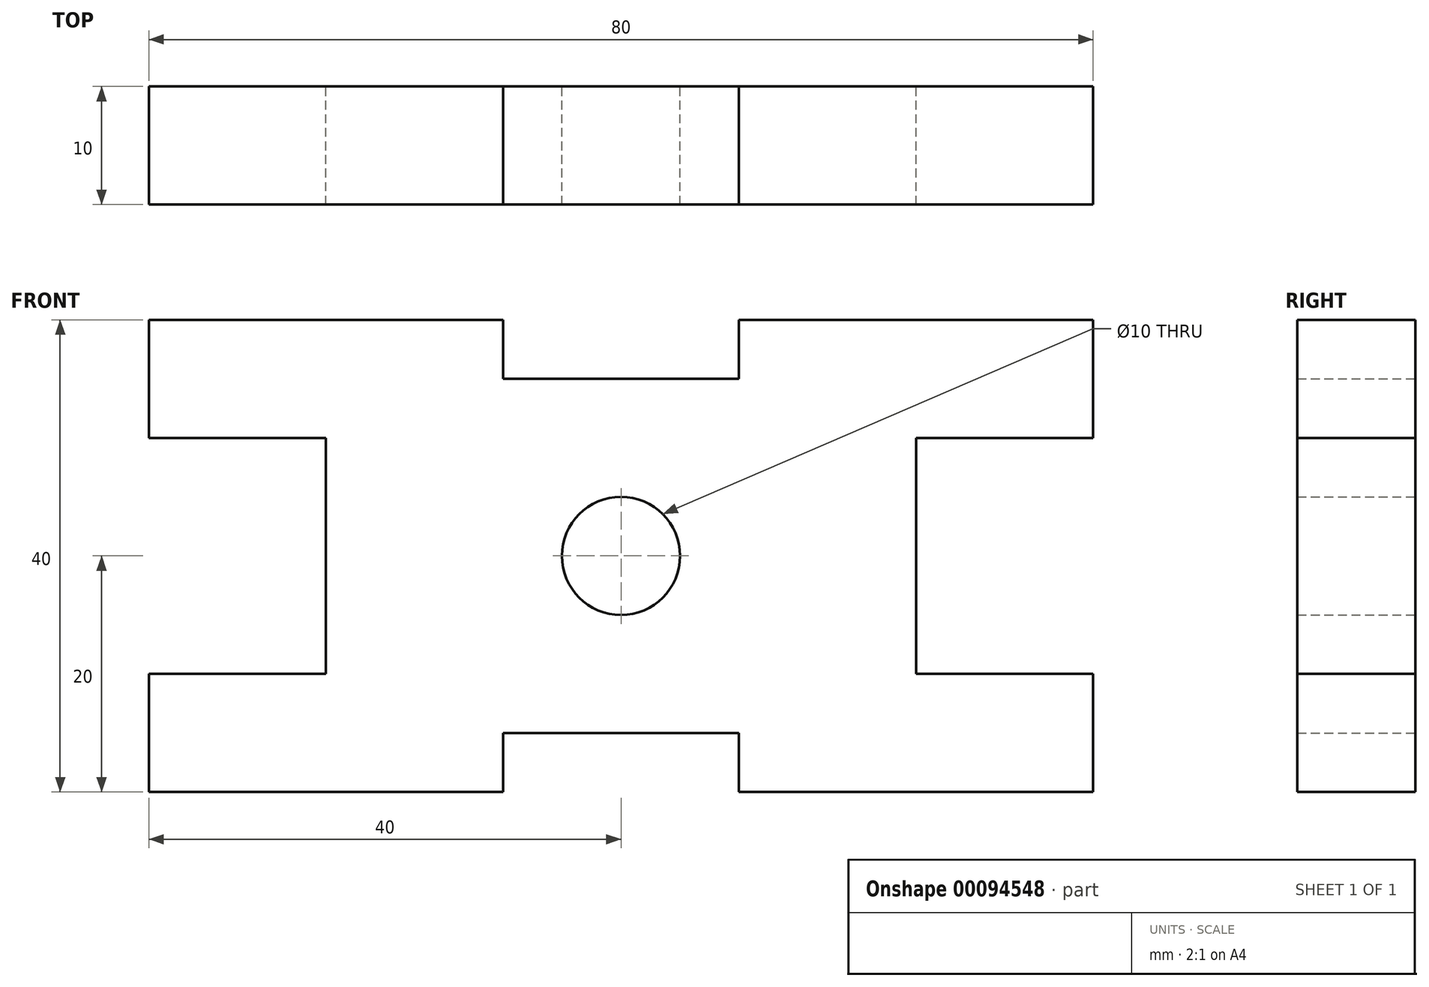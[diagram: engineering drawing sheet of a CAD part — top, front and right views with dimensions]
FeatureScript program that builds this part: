
annotation { "Feature Type Name" : "Feature", "Feature Type Description" : "" }
export const myFeature = defineFeature(function(context is Context, id is Id, definition is map)
    precondition{}
    {
        {
            var Q0;
            Q0=qCreatedBy(makeId("Front.planeOp"),FACE);
            var sketch = newSketch(context, id + "F0", { "sketchPlane" : qUnion([Q0])});
            skLineSegment(sketch, "E0", {"start": v(20, 0) * mm, "end": v(0, 0) * mm});
            skLineSegment(sketch, "E1", {"start": v(0, 0) * mm, "end": v(0, -5) * mm});
            skLineSegment(sketch, "E2", {"start": v(0, -5) * mm, "end": v(-30, -5) * mm});
            skLineSegment(sketch, "E3", {"start": v(-30, -5) * mm, "end": v(-30, 5) * mm});
            skLineSegment(sketch, "E4", {"start": v(-30, 5) * mm, "end": v(-15, 5) * mm});
            skLineSegment(sketch, "E5", {"start": v(-15, 5) * mm, "end": v(-15, 25) * mm});
            skLineSegment(sketch, "E6", {"start": v(-15, 25) * mm, "end": v(-30, 25) * mm});
            skLineSegment(sketch, "E7", {"start": v(-30, 25) * mm, "end": v(-30, 35) * mm});
            skLineSegment(sketch, "E8", {"start": v(-30, 35) * mm, "end": v(0, 35) * mm});
            skLineSegment(sketch, "E9", {"start": v(0, 35) * mm, "end": v(0, 30) * mm});
            skLineSegment(sketch, "E10", {"start": v(0, 30) * mm, "end": v(20, 30) * mm});
            skLineSegment(sketch, "E11", {"start": v(20, 30) * mm, "end": v(20, 35) * mm});
            skLineSegment(sketch, "E12", {"start": v(20, -5) * mm, "end": v(20, 0) * mm});
            skLineSegment(sketch, "E13", {"start": v(20, 35) * mm, "end": v(50, 35) * mm});
            skLineSegment(sketch, "E14", {"start": v(50, 35) * mm, "end": v(50, 25) * mm});
            skLineSegment(sketch, "E15", {"start": v(50, 25) * mm, "end": v(35, 25) * mm});
            skLineSegment(sketch, "E16", {"start": v(35, 25) * mm, "end": v(35, 5) * mm});
            skLineSegment(sketch, "E17", {"start": v(35, 5) * mm, "end": v(50, 5) * mm});
            skLineSegment(sketch, "E18", {"start": v(50, 5) * mm, "end": v(50, -5) * mm});
            skLineSegment(sketch, "E19", {"start": v(50, -5) * mm, "end": v(20, -5) * mm});
            skLineSegment(sketch, "E20", {"start": v(-15, 15) * mm, "end": v(35, 15) * mm, "construction": true});
            skLineSegment(sketch, "E21", {"start": v(10, 30) * mm, "end": v(10, 0) * mm, "construction": true});
            skCircle(sketch, "E22", {"center": v(10, 15) * mm, "radius": 5 * mm});
            skSolve(sketch);
        }
        {
            var Q0;
            Q0 = qSketchRegion(id + "F0", true);
            extrude(context, id + "F1", {"entities" : qUnion([Q0]), "depth" : 10 * mm});
        }
    });
